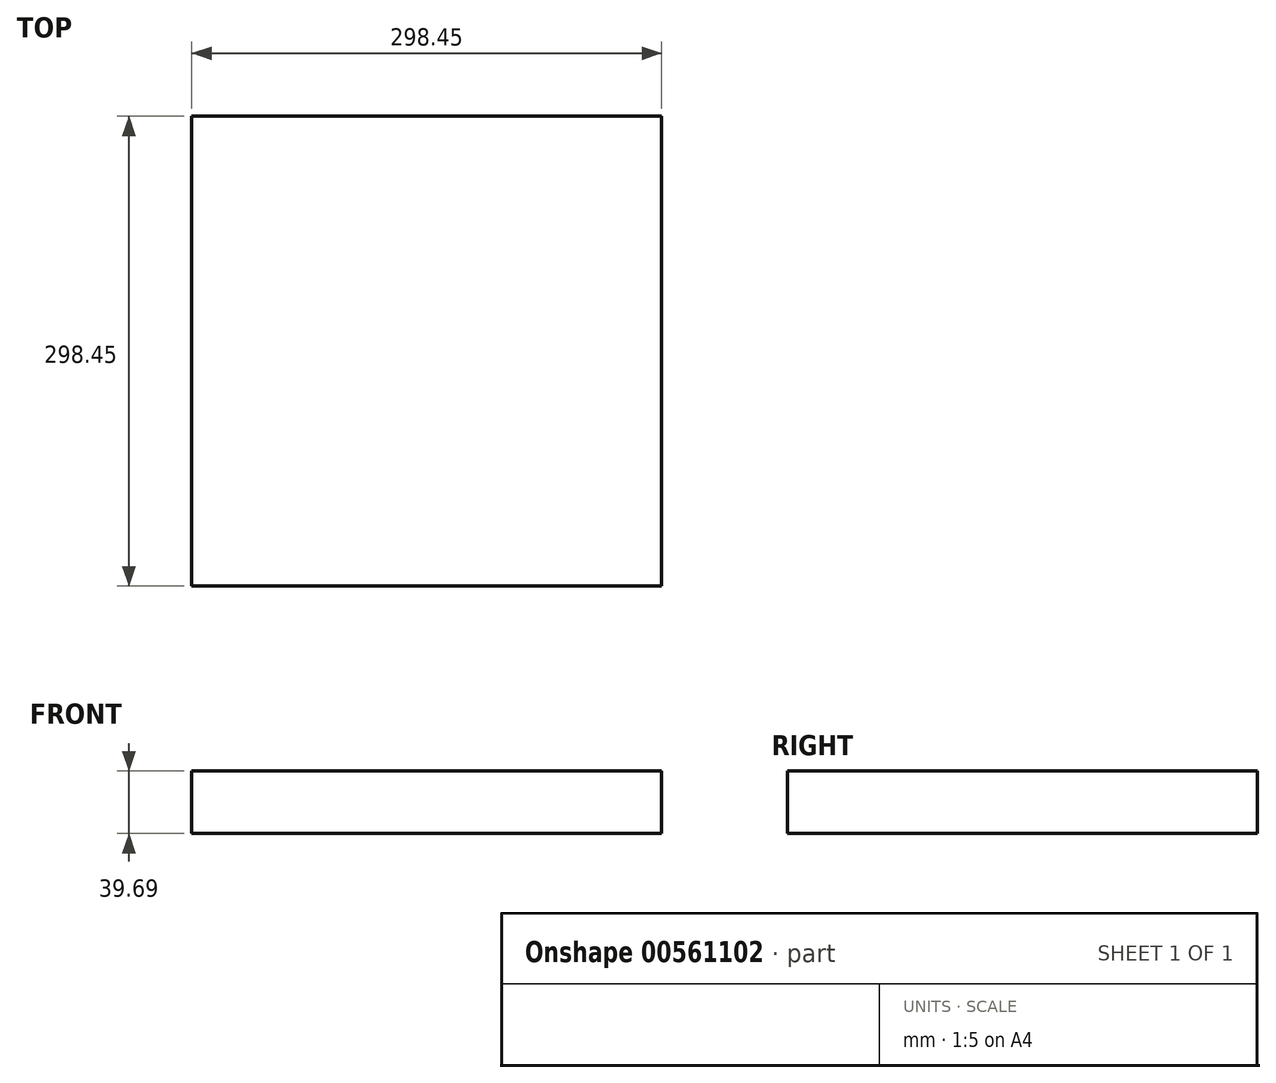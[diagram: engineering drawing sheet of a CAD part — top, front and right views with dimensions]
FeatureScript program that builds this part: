
annotation { "Feature Type Name" : "Feature", "Feature Type Description" : "" }
export const myFeature = defineFeature(function(context is Context, id is Id, definition is map)
    precondition{}
    {
        {
            var Q0;
            Q0=qCreatedBy(makeId("Top.planeOp"),FACE);
            var sketch = newSketch(context, id + "F0", { "sketchPlane" : qUnion([Q0])});
            skLineSegment(sketch, "E0.bottom", {"start": v(0, 0) * mm, "end": v(298.45, 0) * mm});
            skLineSegment(sketch, "E0.top", {"start": v(0, 298.45) * mm, "end": v(298.45, 298.45) * mm});
            skLineSegment(sketch, "E0.left", {"start": v(0, 0) * mm, "end": v(0, 298.45) * mm});
            skLineSegment(sketch, "E0.right", {"start": v(298.45, 0) * mm, "end": v(298.45, 298.45) * mm});
            skSolve(sketch);
        }
        {
            var Q0;
            Q0=makeQuery(id+"F0.imprint","IMPRINT",FACE,{"disambiguationData":[TD([[makeQuery(id+"F0.imprint","IMPRINT",EDGE,{"derivedFrom":sQuery(id+"F0.wireOp",EDGE,"E0.bottom")}),1.0]])]});
            extrude(context, id + "F1", {"entities" : qUnion([Q0]), "depth" : 39.69 * mm, "offsetDistance" : 25.4 * mm});
        }
    });
